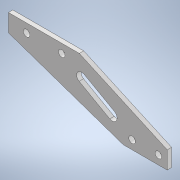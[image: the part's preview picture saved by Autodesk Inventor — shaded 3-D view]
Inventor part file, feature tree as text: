
AUTODESK INVENTOR PART (.ipt)
format: ipt  version: 2020 (Build 240168000, 168)  size: 160,768 bytes
history: native  units: mm
features: other x6, extrude x3, sketch x3, reference x3, projected_geometry x2
ambient origin geometry x8: Origin, YZ Plane, XZ Plane, XY Plane, X Axis, Y Axis, Z Axis, Center Point
bodies: Solid1 (feature_tree)
feature tree (17):
  extrude  "Extrusion1"  Depth=10.0mm
  extrude  "Extrusion3"  Depth=10.0mm
  extrude  "Extrusion4"  Depth=10.0mm
  sketch  "Sketch1"  dims[d0=10.0mm d1=110.0mm]
  reference  "Reference1"
  reference  "Reference2"
  reference  "Reference3"
  sketch  "Sketch3"  dims[d2=32.0mm d3=10.0mm]
  projected_geometry  "Projected Loop2"
  sketch  "Sketch4"  dims[d4=10.0mm d5=20.0mm d6=8.0mm d7=6.0mm d8=3.0mm d9=6.0mm d10=3.0mm d11=2.0mm d12=0.0mm d23=3.0mm d24=3.0mm d25=2.0mm d26=0.0mm d27=8.0mm d28=4.5mm d29=10.0mm d30=0.0mm]
  projected_geometry  "Projected Loop3"
  parser-record x1  (decoder bookkeeping rows leaked as tree rows — omitted from the tree; the rows remain in map.json)
  other  "delta_1.iam"
  other  "arm_holder_1:1"
  other  "arm_1:1"
  other  "arm_shift_1:3"
  other  "pin_8_45:1"
note: 1 file-system path scrubbed to <path> (originals preserved in map.json)
